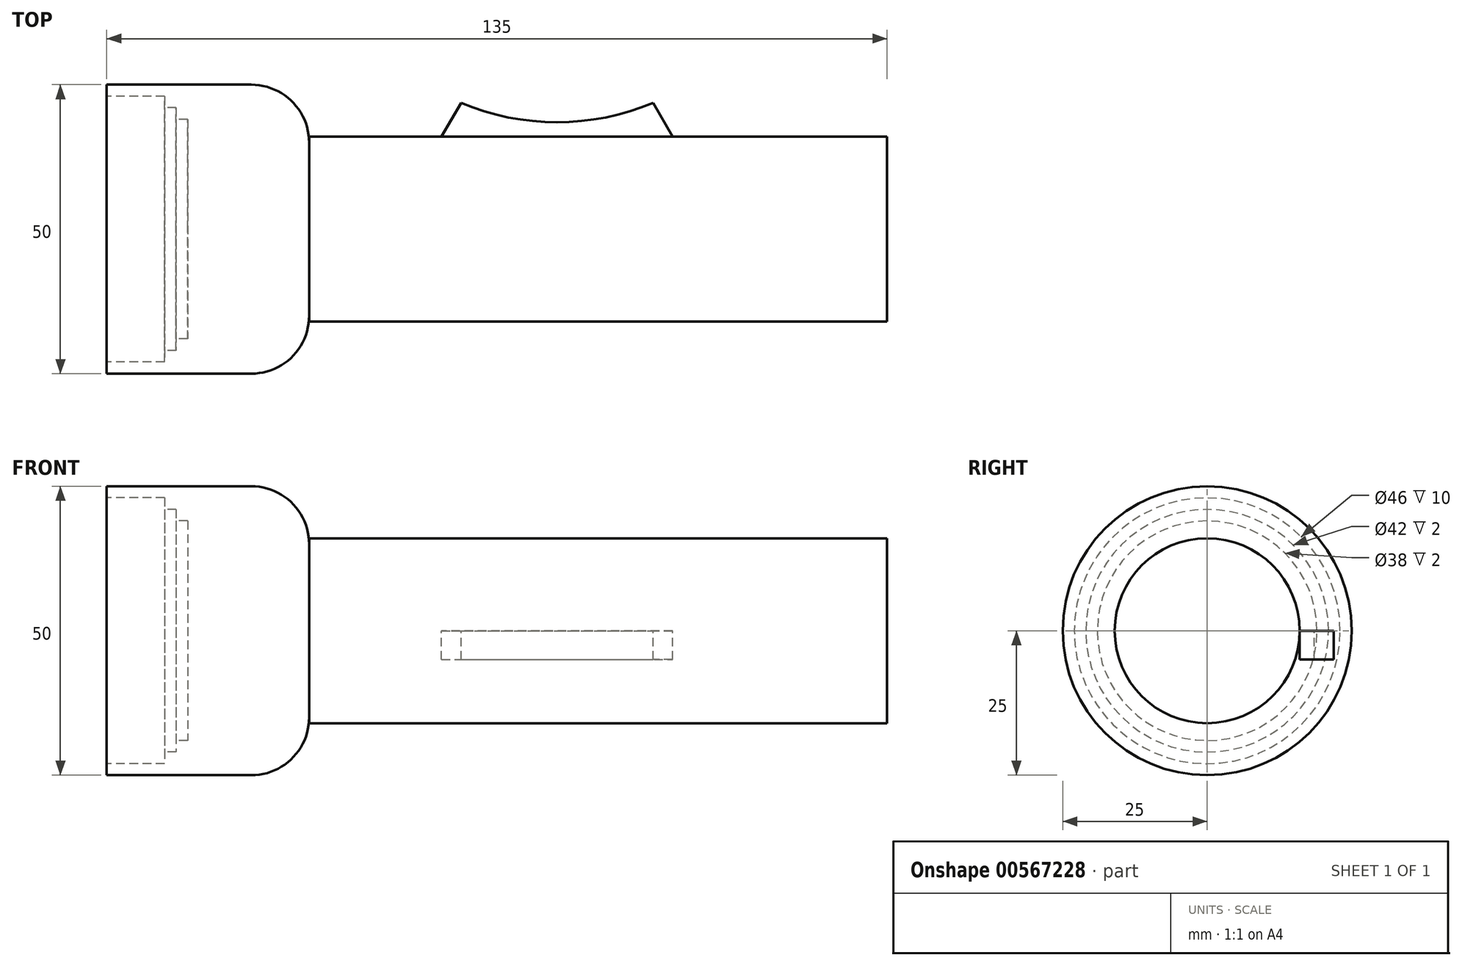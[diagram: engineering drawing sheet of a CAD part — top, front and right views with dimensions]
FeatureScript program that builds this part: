
annotation { "Feature Type Name" : "Feature", "Feature Type Description" : "" }
export const myFeature = defineFeature(function(context is Context, id is Id, definition is map)
    precondition{}
    {
        {
            var Q0;
            Q0=qCreatedBy(makeId("Right.planeOp"),FACE);
            var sketch = newSketch(context, id + "F0", { "sketchPlane" : qUnion([Q0])});
            skCircle(sketch, "E0", {"center": v(0, 0) * mm, "radius": 16 * mm});
            skSolve(sketch);
        }
        {
            var Q0;
            Q0 = qSketchRegion(id + "F0", true);
            extrude(context, id + "F1", {"entities" : qUnion([Q0]), "depth" : 100 * mm, "offsetDistance" : 25 * mm});
        }
        {
            var Q0;
            Q0=makeQuery(id+"F1.opExtrude","CAP_FACE",FACE,{"disambiguationData":[OSD([sQuery(id+"F0.wireOp",EDGE,"E0")])],"isStart":true});
            var sketch = newSketch(context, id + "F2", { "sketchPlane" : qUnion([Q0])});
            skCircle(sketch, "E1", {"center": v(0, 0) * mm, "radius": 25 * mm});
            skSolve(sketch);
        }
        {
            var Q0;
            Q0 = qSketchRegion(id + "F2", true);
            extrude(context, id + "F3", {"entities" : qUnion([Q0]), "depth" : 35 * mm, "offsetDistance" : 25 * mm});
        }
        {
            var Q0;
            Q0=makeQuery(id+"F3.opExtrude","CAP_FACE",FACE,{"disambiguationData":[OSD([sQuery(id+"F2.wireOp",EDGE,"E1")])],"isStart":false});
            var sketch = newSketch(context, id + "F4", { "sketchPlane" : qUnion([Q0])});
            skCircle(sketch, "E2", {"center": v(0, 0) * mm, "radius": 23 * mm});
            skSolve(sketch);
        }
        {
            var Q0;
            Q0=makeQuery(id+"F4.imprint","IMPRINT",FACE,{"disambiguationData":[TD([[makeQuery(id+"F4.imprint","IMPRINT",EDGE,{"derivedFrom":sQuery(id+"F4.wireOp",EDGE,"iOZFOxmd-7CZR-VwlF-P1M4-Ysl6YgwgvStK")}),1.0]])]});
            var Q1;
            Q1=makeQuery(id+"F4.imprint","IMPRINT",FACE,{"disambiguationData":[TD([[makeQuery(id+"F4.imprint","IMPRINT",EDGE,{"derivedFrom":sQuery(id+"F4.wireOp",EDGE,"E2")}),1.0]])]});
            extrude(context, id + "F5", {"entities" : qUnion([Q0, Q1]), "operationType" : NewBodyOperationType.REMOVE, "oppositeDirection" : true, "depth" : 10 * mm, "offsetDistance" : 25 * mm});
        }
        {
            var Q0;
            Q0=makeQuery(id+"F5.boolean.opBoolean","COPY",FACE,{"derivedFrom":makeQuery(id+"F5.opExtrude","CAP_FACE",FACE,{"disambiguationData":[OSD([sQuery(id+"F4.wireOp",EDGE,"E2")])],"isStart":false})});
            var sketch = newSketch(context, id + "F6", { "sketchPlane" : qUnion([Q0])});
            skCircle(sketch, "E3", {"center": v(0, 0) * mm, "radius": 21 * mm});
            skSolve(sketch);
        }
        {
            var Q0;
            Q0=makeQuery(id+"F6.imprint","IMPRINT",FACE,{"disambiguationData":[TD([[makeQuery(id+"F6.imprint","IMPRINT",EDGE,{"derivedFrom":sQuery(id+"F6.wireOp",EDGE,"E3")}),1.0]])]});
            extrude(context, id + "F7", {"entities" : qUnion([Q0]), "operationType" : NewBodyOperationType.REMOVE, "oppositeDirection" : true, "depth" : 2 * mm, "offsetDistance" : 25 * mm});
        }
        {
            var Q0;
            Q0=makeQuery(id+"F7.boolean.opBoolean","COPY",FACE,{"derivedFrom":makeQuery(id+"F7.opExtrude","CAP_FACE",FACE,{"disambiguationData":[OSD([sQuery(id+"F6.wireOp",EDGE,"E3")])],"isStart":false})});
            var sketch = newSketch(context, id + "F8", { "sketchPlane" : qUnion([Q0])});
            skCircle(sketch, "E4", {"center": v(0, 0) * mm, "radius": 19 * mm});
            skSolve(sketch);
        }
        {
            var Q0;
            Q0=makeQuery(id+"F8.imprint","IMPRINT",FACE,{"disambiguationData":[TD([[makeQuery(id+"F8.imprint","IMPRINT",EDGE,{"derivedFrom":sQuery(id+"F8.wireOp",EDGE,"E4")}),1.0]])]});
            extrude(context, id + "F9", {"entities" : qUnion([Q0]), "operationType" : NewBodyOperationType.REMOVE, "oppositeDirection" : true, "depth" : 2 * mm, "offsetDistance" : 25 * mm});
        }
        {
            var Q0;
            Q0=makeQuery(id+"F3.opExtrude","CAP_FACE",FACE,{"disambiguationData":[OSD([sQuery(id+"F2.wireOp",EDGE,"E1")])],"isStart":true});
            fillet(context, id + "F10", {"entities" : qUnion([Q0]), "radius" : 10 * mm, "tangentPropagation" : true, "allowEdgeOverflow" : false});
        }
        {
            var Q0;
            Q0=qCreatedBy(makeId("Top.planeOp"),FACE);
            var sketch = newSketch(context, id + "F11", { "sketchPlane" : qUnion([Q0])});
            skLineSegment(sketch, "E5", {"start": v(-0.11, 16) * mm, "end": v(22.89, 16) * mm, "construction": true});
            skLineSegment(sketch, "E6", {"start": v(22.89, 16) * mm, "end": v(62.89, 16) * mm, "construction": true});
            skLineSegment(sketch, "E7", {"start": v(62.89, 16) * mm, "end": v(122.89, 16) * mm, "construction": true});
            skLineSegment(sketch, "E8", {"start": v(22.89, 16) * mm, "end": v(42.89, 16) * mm, "construction": true});
            skLineSegment(sketch, "E9", {"start": v(42.89, 34.65) * mm, "end": v(22.89, 34.65) * mm, "construction": true});
            skLineSegment(sketch, "E10", {"start": v(42.89, 16) * mm, "end": v(42.89, 61) * mm, "construction": true});
            skArc(sketch, "E11", {"start": v(26.28, 21.88) * mm, "mid": v(42.89, 18.5) * mm, "end": v(59.5, 21.88) * mm});
            skLineSegment(sketch, "E12", {"start": v(22.89, 16) * mm, "end": v(62.89, 16) * mm});
            skLineSegment(sketch, "E13", {"start": v(22.89, 16) * mm, "end": v(26.28, 21.88) * mm});
            skLineSegment(sketch, "E14", {"start": v(62.89, 16) * mm, "end": v(59.5, 21.88) * mm});
            skSolve(sketch);
        }
        {
            var Q0;
            Q0 = qSketchRegion(id + "F11", true);
            extrude(context, id + "F12", {"entities" : qUnion([Q0]), "operationType" : NewBodyOperationType.ADD, "oppositeDirection" : true, "depth" : 5 * mm, "offsetDistance" : 25 * mm});
        }
    });
